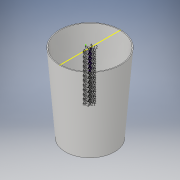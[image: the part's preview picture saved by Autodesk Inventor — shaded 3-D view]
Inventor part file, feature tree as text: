
AUTODESK INVENTOR PART (.ipt)
format: ipt  version: 2017 (Build 210142000, 142)  size: 217,600 bytes
history: native  units: in
note: dims shown in document units (in); Inventor stores cm internally (conversion verified against a paired STEP export)
features: sketch x2, revolve x1
ambient origin geometry x8: Origin, YZ Plane, XZ Plane, XY Plane, X Axis, Y Axis, Z Axis, Center Point
bodies: Solid1 (feature_tree)
feature tree (3):
  revolve  "Revolution1"  [1 undecoded]
  sketch  "Sketch2"  dims[d2=0.4167in d3=0.012in d4=0.012in d5=90.0deg d6=0.0208in d8=0.0208in d11=0.012in d12=0.012in d23=0.0208in d24=0.0208in d25=0.012in d26=0.012in d27=0.012in d28=0.0208in d29=0.0208in d30=0.012in d31=0.0208in d32=0.0208in d33=0.012in d34=0.012in d35=0.012in d36=0.012in d37=0.012in d38=0.0208in d39=0.0208in d40=0.012in d41=0.0208in d42=0.0208in d43=0.012in d44=0.012in d45=0.0208in d46=0.0208in d47=0.012in d48=0.0208in d49=0.0208in d50=0.012in d51=0.012in d52=0.012in d53=0.012in d54=0.012in d55=0.012in d56=0.012in d57=0.012in d58=0.0208in d59=0.0208in d60=0.012in d61=0.0208in d62=0.0208in d63=0.012in d64=0.012in d65=0.0208in d66=0.0208in d67=0.012in d68=0.0208in d69=0.0208in d70=0.012in d71=0.012in d72=0.012in d89=0.012in d90=0.012in d91=0.012in d92=0.012in d97=0.012in]
  sketch  "Sketch1"  dims[d0=1.0833in d1=0.3333in]
note: 1 required parameter value undecoded (feature->parameter linkage not recoverable at this tier; creation-order binding heuristic only, values carry confidence <= 0.55)
